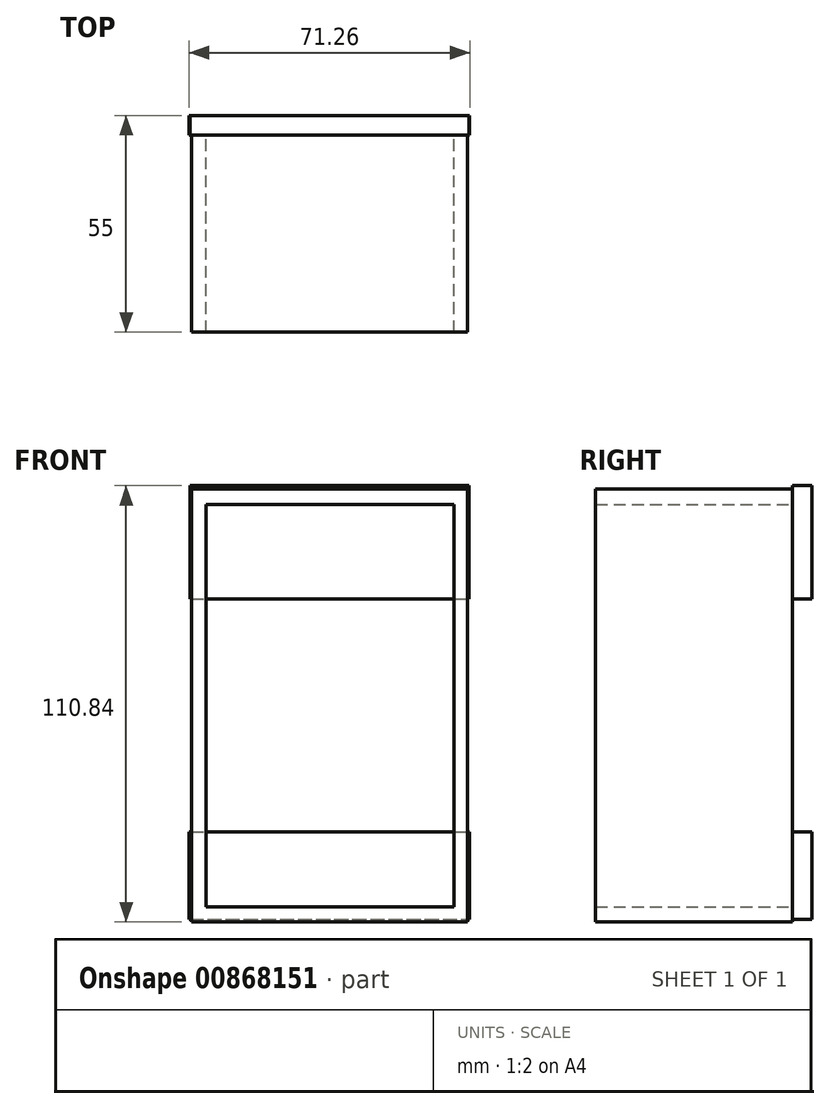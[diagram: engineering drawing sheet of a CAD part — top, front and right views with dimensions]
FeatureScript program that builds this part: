
annotation { "Feature Type Name" : "Feature", "Feature Type Description" : "" }
export const myFeature = defineFeature(function(context is Context, id is Id, definition is map)
    precondition{}
    {
        {
            var Q0;
            Q0=qCreatedBy(makeId("Front.planeOp"),FACE);
            var sketch = newSketch(context, id + "F0", { "sketchPlane" : qUnion([Q0])});
            skLineSegment(sketch, "E0.bottom", {"start": v(-35.75, 55.53) * mm, "end": v(34.25, 55.53) * mm});
            skLineSegment(sketch, "E0.top", {"start": v(-35.75, -54.47) * mm, "end": v(34.25, -54.47) * mm});
            skLineSegment(sketch, "E0.left", {"start": v(-35.75, 55.53) * mm, "end": v(-35.75, -54.47) * mm});
            skLineSegment(sketch, "E0.right", {"start": v(34.25, 55.53) * mm, "end": v(34.25, -54.47) * mm});
            skLineSegment(sketch, "E1.bottom", {"start": v(-32.13, 51.62) * mm, "end": v(30.87, 51.62) * mm});
            skLineSegment(sketch, "E1.top", {"start": v(-32.13, -50.63) * mm, "end": v(30.87, -50.63) * mm});
            skLineSegment(sketch, "E1.left", {"start": v(-32.13, 51.62) * mm, "end": v(-32.13, -50.63) * mm});
            skLineSegment(sketch, "E1.right", {"start": v(30.87, 51.62) * mm, "end": v(30.87, -50.63) * mm});
            skLineSegment(sketch, "E2.top", {"start": v(-35.75, 35.21) * mm, "end": v(34.25, 35.21) * mm});
            skLineSegment(sketch, "E2.left", {"start": v(-35.75, 55.53) * mm, "end": v(-35.75, 35.21) * mm});
            skLineSegment(sketch, "E2.right", {"start": v(34.25, 55.53) * mm, "end": v(34.25, 35.21) * mm});
            skLineSegment(sketch, "E3.bottom", {"start": v(-35.75, -35.97) * mm, "end": v(34.25, -35.97) * mm});
            skLineSegment(sketch, "E3.left", {"start": v(-35.75, -35.97) * mm, "end": v(-35.75, -54.47) * mm});
            skLineSegment(sketch, "E3.right", {"start": v(34.25, -35.97) * mm, "end": v(34.25, -54.47) * mm});
            skSolve(sketch);
        }
        {
            var Q0;
            Q0 = qSketchRegion(id + "F0", true);
            extrude(context, id + "F1", {"entities" : qUnion([Q0]), "depth" : 50 * mm, "offsetDistance" : 25 * mm});
        }
        {
            var Q0;
            Q0 = qSketchRegion(id + "F0", true);
            extrude(context, id + "F2", {"entities" : qUnion([Q0]), "operationType" : NewBodyOperationType.ADD, "depth" : 25 * mm, "offsetDistance" : 25 * mm});
        }
        {
            var Q0;
            Q0=qCreatedBy(makeId("Front.planeOp"),FACE);
            var sketch = newSketch(context, id + "F3", { "sketchPlane" : qUnion([Q0])});
            skLineSegment(sketch, "E4.bottom", {"start": v(-36.13, 56.37) * mm, "end": v(34.63, 56.37) * mm});
            skLineSegment(sketch, "E4.top", {"start": v(-36.13, 27.62) * mm, "end": v(34.63, 27.62) * mm});
            skLineSegment(sketch, "E4.left", {"start": v(-36.13, 56.37) * mm, "end": v(-36.13, 27.62) * mm});
            skLineSegment(sketch, "E4.right", {"start": v(34.63, 56.37) * mm, "end": v(34.63, 27.62) * mm});
            skLineSegment(sketch, "E5.bottom", {"start": v(-36.38, -31.63) * mm, "end": v(34.88, -31.63) * mm});
            skLineSegment(sketch, "E5.top", {"start": v(-36.38, -53.88) * mm, "end": v(34.88, -53.88) * mm});
            skLineSegment(sketch, "E5.left", {"start": v(-36.38, -31.63) * mm, "end": v(-36.38, -53.88) * mm});
            skLineSegment(sketch, "E5.right", {"start": v(34.88, -31.63) * mm, "end": v(34.88, -53.88) * mm});
            skSolve(sketch);
        }
        {
            var Q0;
            Q0 = qSketchRegion(id + "F3", true);
            extrude(context, id + "F4", {"entities" : qUnion([Q0]), "operationType" : NewBodyOperationType.ADD, "oppositeDirection" : true, "depth" : 5 * mm, "offsetDistance" : 25 * mm});
        }
    });
